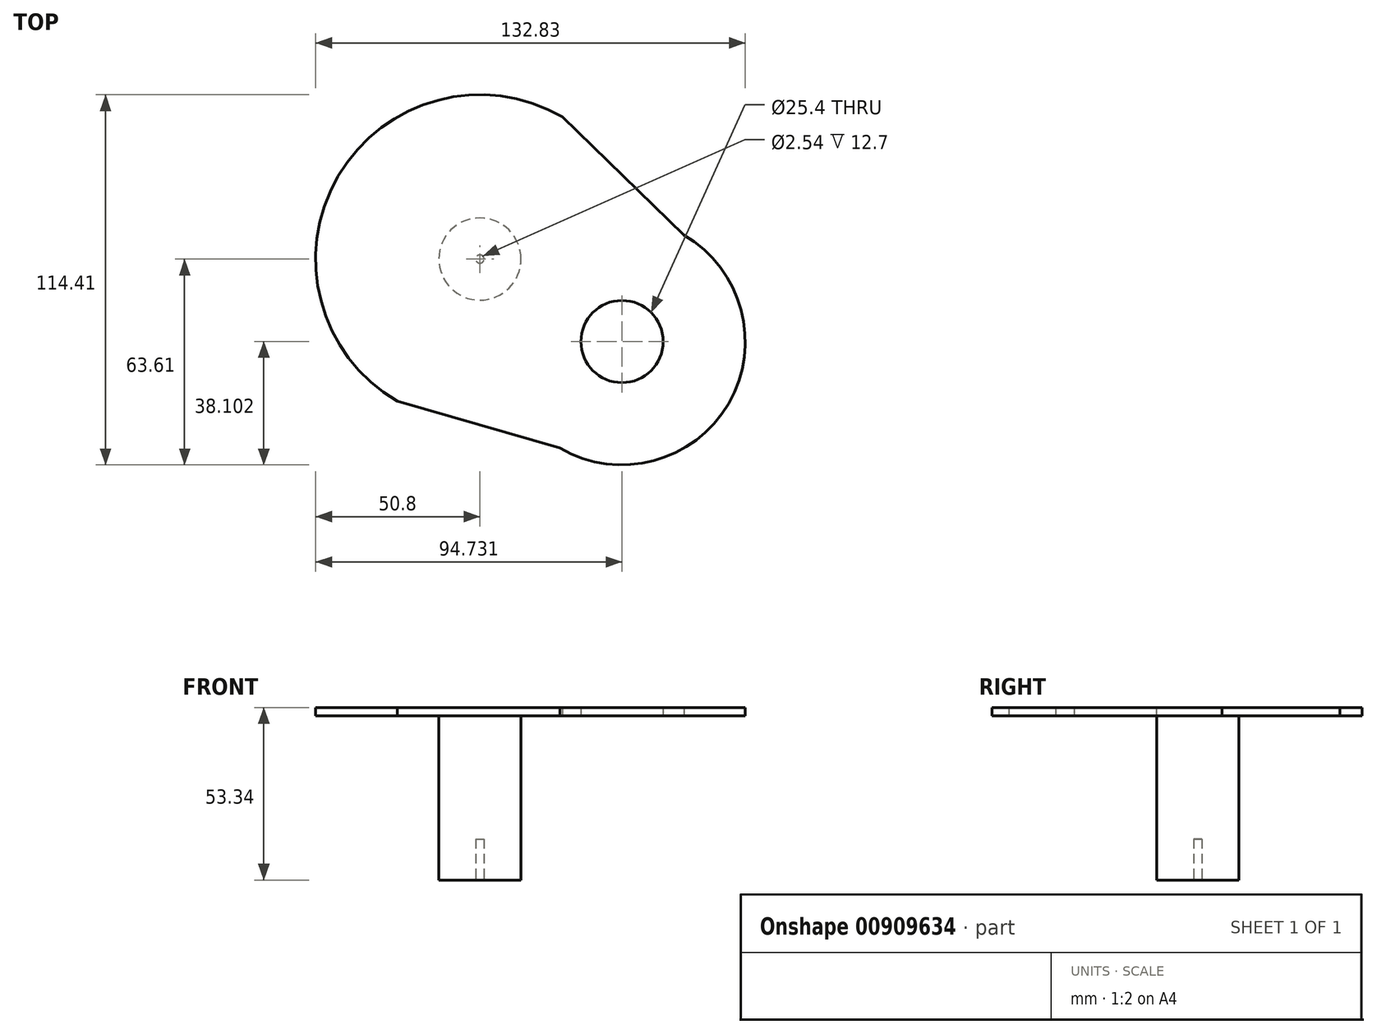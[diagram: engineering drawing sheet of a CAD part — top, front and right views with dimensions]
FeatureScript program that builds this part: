
annotation { "Feature Type Name" : "Feature", "Feature Type Description" : "" }
export const myFeature = defineFeature(function(context is Context, id is Id, definition is map)
    precondition{}
    {
        {
            var Q0;
            Q0=qCreatedBy(makeId("Top.planeOp"),FACE);
            var sketch = newSketch(context, id + "F0", { "sketchPlane" : qUnion([Q0])});
            skCircle(sketch, "E0", {"center": v(0, 0) * mm, "radius": 12.7 * mm});
            skSolve(sketch);
        }
        {
            var Q0;
            Q0 = qSketchRegion(id + "F0", true);
            extrude(context, id + "F1", {"entities" : qUnion([Q0]), "depth" : 50.8 * mm, "offsetDistance" : 25.4 * mm});
        }
        {
            var Q0;
            Q0=makeQuery(id+"F1.opExtrude","CAP_FACE",FACE,{"disambiguationData":[OSD([sQuery(id+"F0.wireOp",EDGE,"E0")])],"isStart":false});
            var sketch = newSketch(context, id + "F2", { "sketchPlane" : qUnion([Q0])});
            skCircle(sketch, "E1", {"center": v(0, 0) * mm, "radius": 50.8 * mm});
            skCircle(sketch, "E2", {"center": v(43.93, -25.5) * mm, "radius": 38.1 * mm});
            skLineSegment(sketch, "E3", {"start": v(43.93, -25.5) * mm, "end": v(0, 0) * mm, "construction": true});
            skLineSegment(sketch, "E4", {"start": v(0, 0) * mm, "end": v(25.5, 43.93) * mm, "construction": true});
            skLineSegment(sketch, "E5", {"start": v(25.5, 43.93) * mm, "end": v(-25.5, -43.93) * mm, "construction": true});
            skLineSegment(sketch, "E6", {"start": v(43.93, -25.5) * mm, "end": v(63.06, 7.44) * mm, "construction": true});
            skLineSegment(sketch, "E7", {"start": v(63.06, 7.44) * mm, "end": v(24.8, -58.46) * mm, "construction": true});
            skLineSegment(sketch, "E8", {"start": v(24.8, -58.46) * mm, "end": v(-25.5, -43.93) * mm});
            skLineSegment(sketch, "E9", {"start": v(63.06, 7.44) * mm, "end": v(25.5, 43.93) * mm});
            skCircle(sketch, "E10", {"center": v(43.93, -25.5) * mm, "radius": 12.7 * mm});
            skSolve(sketch);
        }
        {
            var Q0;
            {var subQ5=makeQuery(id+"F1.opExtrude","CAP_EDGE",EDGE,{"disambiguationData":[OSD([sQuery(id+"F0.wireOp",EDGE,"E0")])],"isStart":false});Q0=makeQuery(id+"F2.imprint","IMPRINT",FACE,{"disambiguationData":[TD([[makeQuery(id+"F2.imprint","IMPRINT",EDGE,{"derivedFrom":subQ5}),-1.0]])]});}
            var Q1;
            {var subQ0=sQuery(id+"F2.wireOp",EDGE,"E2");var subQ1=sQuery(id+"F2.wireOp",EDGE,"E1");var subQ2=makeQuery(id+"F2.imprint","INTERSECT",VERTEX,{"disambiguationData":[OD(0.0)],"derivedFrom":[subQ1,subQ0]});Q1=makeQuery(id+"F2.imprint","IMPRINT",FACE,{"disambiguationData":[TD([[makeQuery(id+"F2.imprint","IMPRINT",EDGE,{"disambiguationData":[TD([[subQ2,1.0]])],"derivedFrom":subQ1}),1.0]])]});}
            var Q2;
            {var subQ0=sQuery(id+"F2.wireOp",EDGE,"E9");var subQ1=sQuery(id+"F2.wireOp",EDGE,"E1");var subQ2=makeQuery(id+"F2.imprint","INTERSECT",VERTEX,{"disambiguationData":[OD(1.0)],"derivedFrom":[subQ1,subQ0]});Q2=makeQuery(id+"F2.imprint","IMPRINT",FACE,{"disambiguationData":[TD([[makeQuery(id+"F2.imprint","IMPRINT",EDGE,{"disambiguationData":[TD([[subQ2,1.0]])],"derivedFrom":subQ1}),-1.0]])]});}
            var Q3;
            {var subQ0=sQuery(id+"F2.wireOp",EDGE,"E2");var subQ1=sQuery(id+"F2.wireOp",EDGE,"E1");var subQ2=makeQuery(id+"F2.imprint","INTERSECT",VERTEX,{"disambiguationData":[OD(0.0)],"derivedFrom":[subQ1,subQ0]});Q3=makeQuery(id+"F2.imprint","IMPRINT",FACE,{"disambiguationData":[TD([[makeQuery(id+"F2.imprint","IMPRINT",EDGE,{"disambiguationData":[TD([[subQ2,1.0]])],"derivedFrom":subQ1}),-1.0]])]});}
            var Q4;
            {var subQ0=sQuery(id+"F2.wireOp",EDGE,"E8");var subQ1=sQuery(id+"F2.wireOp",EDGE,"E1");var subQ2=makeQuery(id+"F2.imprint","INTERSECT",VERTEX,{"disambiguationData":[OD(1.0)],"derivedFrom":[subQ1,subQ0]});Q4=makeQuery(id+"F2.imprint","IMPRINT",FACE,{"disambiguationData":[TD([[makeQuery(id+"F2.imprint","IMPRINT",EDGE,{"disambiguationData":[TD([[subQ2,-1.0]])],"derivedFrom":subQ1}),-1.0]])]});}
            var Q5;
            Q5=makeQuery(id+"F2.imprint","IMPRINT",FACE,{"disambiguationData":[TD([[makeQuery(id+"F2.imprint","IMPRINT",EDGE,{"derivedFrom":makeQuery(id+"F1.opExtrude","CAP_EDGE",EDGE,{"disambiguationData":[OSD([sQuery(id+"F0.wireOp",EDGE,"E0")])],"isStart":false})}),1.0]])]});
            extrude(context, id + "F3", {"entities" : qUnion([Q0, Q1, Q2, Q3, Q4, Q5]), "operationType" : NewBodyOperationType.ADD, "depth" : 2.54 * mm, "offsetDistance" : 25.4 * mm});
        }
        {
            var Q0;
            Q0=makeQuery(id+"F1.opExtrude","CAP_FACE",FACE,{"disambiguationData":[OSD([sQuery(id+"F0.wireOp",EDGE,"E0")])],"isStart":true});
            var sketch = newSketch(context, id + "F4", { "sketchPlane" : qUnion([Q0])});
            skCircle(sketch, "E11", {"center": v(0, 0) * mm, "radius": 1.27 * mm});
            skSolve(sketch);
        }
        {
            var Q0;
            Q0 = qSketchRegion(id + "F4", true);
            extrude(context, id + "F5", {"entities" : qUnion([Q0]), "operationType" : NewBodyOperationType.REMOVE, "oppositeDirection" : true, "depth" : 12.7 * mm, "offsetDistance" : 25.4 * mm});
        }
    });
